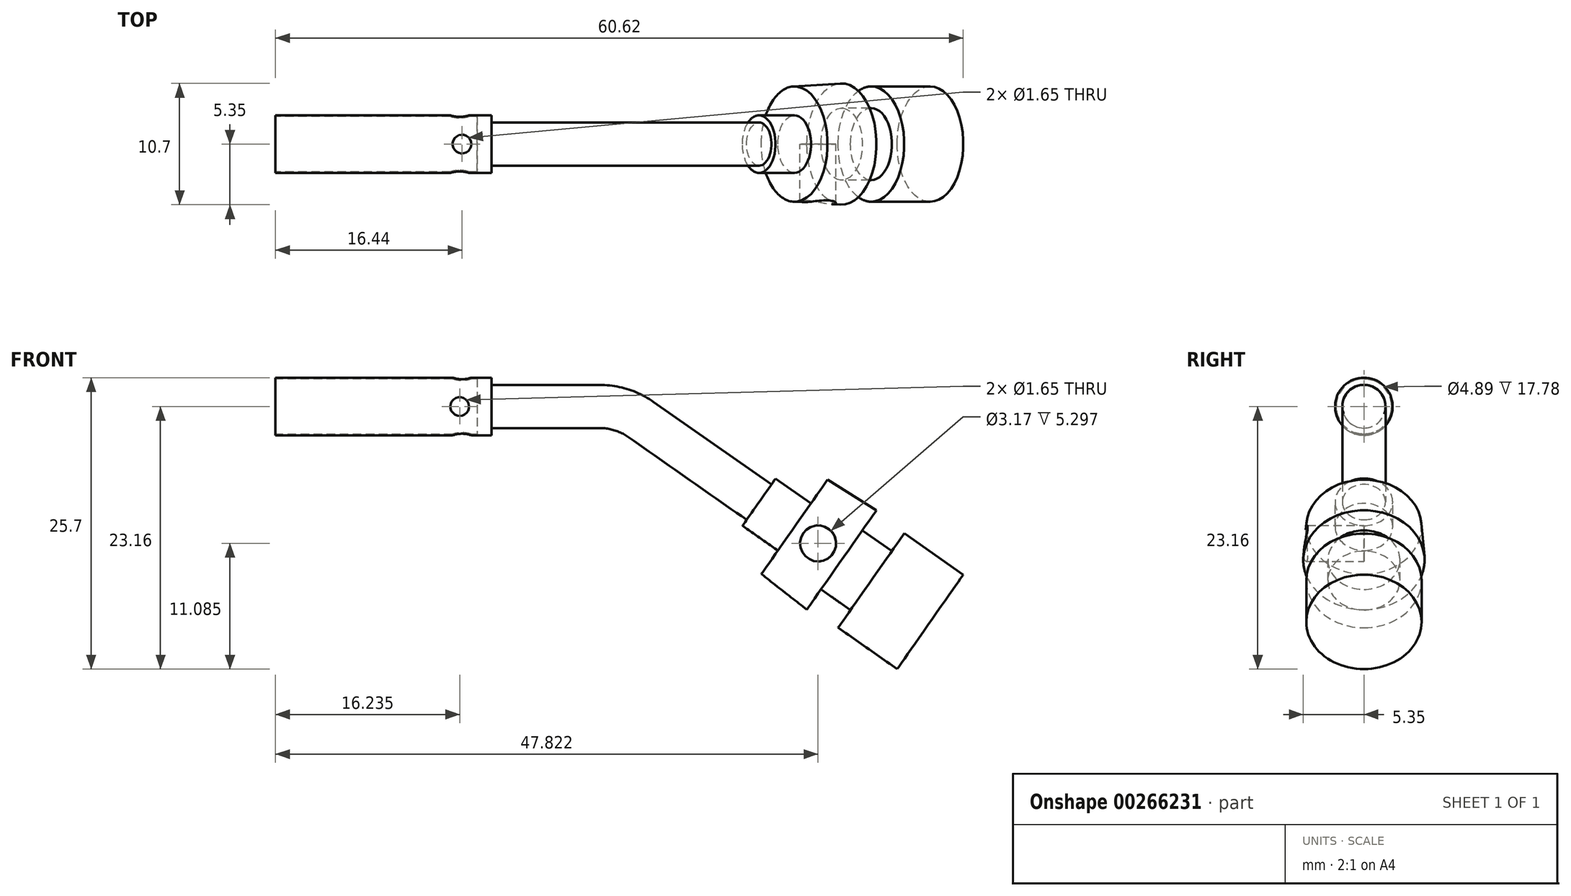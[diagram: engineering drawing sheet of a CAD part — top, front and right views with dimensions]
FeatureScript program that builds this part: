
annotation { "Feature Type Name" : "Feature", "Feature Type Description" : "" }
export const myFeature = defineFeature(function(context is Context, id is Id, definition is map)
    precondition{}
    {
        {
            var Q0;
            Q0=qCreatedBy(makeId("Right.planeOp"),FACE);
            var sketch = newSketch(context, id + "F0", { "sketchPlane" : qUnion([Q0])});
            skCircle(sketch, "E0", {"center": v(0, 0) * mm, "radius": 2.54 * mm});
            skSolve(sketch);
        }
        {
            var Q0;
            Q0=makeQuery(id+"F0.imprint","IMPRINT",FACE,{"disambiguationData":[TD([[makeQuery(id+"F0.imprint","IMPRINT",EDGE,{"derivedFrom":sQuery(id+"F0.wireOp",EDGE,"E0")}),1.0]])]});
            extrude(context, id + "F1", {"entities" : qUnion([Q0]), "depth" : 19.05 * mm});
        }
        {
            var Q0;
            Q0=makeQuery(id+"F1.opExtrude","CAP_FACE",FACE,{"disambiguationData":[OSD([sQuery(id+"F0.wireOp",EDGE,"E0")])],"isStart":false});
            var sketch = newSketch(context, id + "F2", { "sketchPlane" : qUnion([Q0])});
            skCircle(sketch, "E1", {"center": v(0, 0) * mm, "radius": 1.9 * mm});
            skSolve(sketch);
        }
        {
            var Q0;
            Q0=qCreatedBy(makeId("Front.planeOp"),FACE);
            var sketch = newSketch(context, id + "F3", { "sketchPlane" : qUnion([Q0])});
            skLineSegment(sketch, "E2.0", {"start": v(19.05, 2.54) * mm, "end": v(19.05, -2.54) * mm, "construction": true});
            skLineSegment(sketch, "E3", {"start": v(19.05, 0) * mm, "end": v(28.58, 0) * mm});
            skArc(sketch, "E4", {"start": v(32.22, -1.15) * mm, "mid": v(30.48, -0.3) * mm, "end": v(28.58, 0) * mm});
            skLineSegment(sketch, "E5", {"start": v(32.22, -1.15) * mm, "end": v(42.62, -8.43) * mm});
            skSolve(sketch);
        }
        {
            var Q0;
            Q0=makeQuery(id+"F2.imprint","IMPRINT",FACE,{"disambiguationData":[TD([[makeQuery(id+"F2.imprint","IMPRINT",EDGE,{"derivedFrom":sQuery(id+"F2.wireOp",EDGE,"E1")}),1.0]])]});
            var Q1;
            Q1=sQuery(id+"F3.wireOp",EDGE,"E3");
            var Q2;
            Q2=sQuery(id+"F3.wireOp",EDGE,"E4");
            var Q3;
            Q3=sQuery(id+"F3.wireOp",EDGE,"E5");
            sweep(context, id + "F4", {"operationType" : NewBodyOperationType.ADD, "profiles" : qUnion([Q0]), "path" : qUnion([Q1, Q2, Q3])});
        }
        {
            var Q0;
            Q0=makeQuery(id+"F4.opSweep","CAP_FACE",FACE,{"disambiguationData":[OSD([sQuery(id+"F2.wireOp",EDGE,"E1"),sQuery(id+"F3.wireOp",VERTEX,"E5.end")])],"isStart":false});
            var sketch = newSketch(context, id + "F5", { "sketchPlane" : qUnion([Q0])});
            skCircle(sketch, "E6", {"center": v(0, 17.54) * mm, "radius": 2.54 * mm});
            skSolve(sketch);
        }
        {
            var Q0;
            Q0=makeQuery(id+"F5.imprint","IMPRINT",FACE,{"disambiguationData":[TD([[makeQuery(id+"F5.imprint","IMPRINT",EDGE,{"derivedFrom":sQuery(id+"F5.wireOp",EDGE,"E6")}),1.0]])]});
            var Q1;
            Q1=makeQuery(id+"F5.imprint","IMPRINT",FACE,{"disambiguationData":[TD([[makeQuery(id+"F5.imprint","IMPRINT",EDGE,{"derivedFrom":makeQuery(id+"F4.opSweep","CAP_EDGE",EDGE,{"disambiguationData":[OSD([sQuery(id+"F2.wireOp",EDGE,"E1"),sQuery(id+"F3.wireOp",VERTEX,"E5.end")])],"isStart":false})}),1.0]])]});
            extrude(context, id + "F6", {"entities" : qUnion([Q0, Q1]), "operationType" : NewBodyOperationType.ADD, "depth" : 3.8 * mm});
        }
        {
            var Q0;
            Q0=makeQuery(id+"F6.opExtrude","CAP_FACE",FACE,{"disambiguationData":[OSD([sQuery(id+"F5.wireOp",EDGE,"E6")])],"isStart":false});
            var sketch = newSketch(context, id + "F7", { "sketchPlane" : qUnion([Q0])});
            skCircle(sketch, "E7", {"center": v(0, 17.54) * mm, "radius": 5.08 * mm});
            skSolve(sketch);
        }
        {
            var Q0;
            Q0=makeQuery(id+"F7.imprint","IMPRINT",FACE,{"disambiguationData":[TD([[makeQuery(id+"F7.imprint","IMPRINT",EDGE,{"derivedFrom":makeQuery(id+"F6.opExtrude","CAP_EDGE",EDGE,{"disambiguationData":[OSD([sQuery(id+"F5.wireOp",EDGE,"E6")])],"isStart":false})}),1.0]])]});
            var Q1;
            Q1=makeQuery(id+"F7.imprint","IMPRINT",FACE,{"disambiguationData":[TD([[makeQuery(id+"F7.imprint","IMPRINT",EDGE,{"derivedFrom":sQuery(id+"F7.wireOp",EDGE,"E7")}),1.0]])]});
            extrude(context, id + "F8", {"entities" : qUnion([Q0, Q1]), "operationType" : NewBodyOperationType.ADD, "depth" : 5.08 * mm, "hasDraft" : true, "draftAngle" : 3 * degree});
        }
        {
            var Q0;
            Q0=makeQuery(id+"F8.opExtrude","CAP_FACE",FACE,{"disambiguationData":[OSD([sQuery(id+"F7.wireOp",EDGE,"E7")])],"isStart":false});
            var sketch = newSketch(context, id + "F9", { "sketchPlane" : qUnion([Q0])});
            skCircle(sketch, "E8", {"center": v(0, 17.54) * mm, "radius": 3.18 * mm});
            skSolve(sketch);
        }
        {
            var Q0;
            Q0=makeQuery(id+"F9.imprint","IMPRINT",FACE,{"disambiguationData":[TD([[makeQuery(id+"F9.imprint","IMPRINT",EDGE,{"derivedFrom":sQuery(id+"F9.wireOp",EDGE,"E8")}),1.0]])]});
            extrude(context, id + "F10", {"entities" : qUnion([Q0]), "operationType" : NewBodyOperationType.ADD, "depth" : 3.17 * mm});
        }
        {
            var Q0;
            Q0=makeQuery(id+"F10.opExtrude","CAP_FACE",FACE,{"disambiguationData":[OSD([sQuery(id+"F9.wireOp",EDGE,"E8")])],"isStart":false});
            var sketch = newSketch(context, id + "F11", { "sketchPlane" : qUnion([Q0])});
            skCircle(sketch, "E9", {"center": v(0, 17.54) * mm, "radius": 5.08 * mm});
            skSolve(sketch);
        }
        {
            var Q0;
            Q0=makeQuery(id+"F11.imprint","IMPRINT",FACE,{"disambiguationData":[TD([[makeQuery(id+"F11.imprint","IMPRINT",EDGE,{"derivedFrom":sQuery(id+"F11.wireOp",EDGE,"E9")}),1.0]])]});
            var Q1;
            Q1=makeQuery(id+"F11.imprint","IMPRINT",FACE,{"disambiguationData":[TD([[makeQuery(id+"F11.imprint","IMPRINT",EDGE,{"derivedFrom":makeQuery(id+"F10.opExtrude","CAP_EDGE",EDGE,{"disambiguationData":[OSD([sQuery(id+"F9.wireOp",EDGE,"E8")])],"isStart":false})}),1.0]])]});
            extrude(context, id + "F12", {"entities" : qUnion([Q0, Q1]), "operationType" : NewBodyOperationType.ADD, "depth" : 6.35 * mm});
        }
        {
            var Q0;
            Q0=makeQuery(id+"F1.opExtrude","CAP_FACE",FACE,{"disambiguationData":[OSD([sQuery(id+"F0.wireOp",EDGE,"E0")])],"isStart":true});
            var sketch = newSketch(context, id + "F13", { "sketchPlane" : qUnion([Q0])});
            skCircle(sketch, "E10", {"center": v(0, 0) * mm, "radius": 2.44 * mm});
            skSolve(sketch);
        }
        {
            var Q0;
            Q0=makeQuery(id+"F13.imprint","IMPRINT",FACE,{"disambiguationData":[TD([[makeQuery(id+"F13.imprint","IMPRINT",EDGE,{"derivedFrom":sQuery(id+"F13.wireOp",EDGE,"E10")}),1.0]])]});
            extrude(context, id + "F14", {"entities" : qUnion([Q0]), "operationType" : NewBodyOperationType.REMOVE, "oppositeDirection" : true, "depth" : 17.78 * mm});
        }
        {
            var Q0;
            Q0=qCreatedBy(makeId("Top.planeOp"),FACE);
            var sketch = newSketch(context, id + "F15", { "sketchPlane" : qUnion([Q0])});
            skLineSegment(sketch, "E11", {"start": v(0, 2.54) * mm, "end": v(18.98, 2.54) * mm, "construction": true});
            skLineSegment(sketch, "E12", {"start": v(19.05, -2.54) * mm, "end": v(0, -2.54) * mm, "construction": true});
            skCircle(sketch, "E13", {"center": v(16.44, 0) * mm, "radius": 0.83 * mm});
            skSolve(sketch);
        }
        {
            var Q0;
            Q0=makeQuery(id+"F15.imprint","IMPRINT",FACE,{"disambiguationData":[TD([[makeQuery(id+"F15.imprint","IMPRINT",EDGE,{"derivedFrom":sQuery(id+"F15.wireOp",EDGE,"E13")}),1.0]])]});
            extrude(context, id + "F16", {"entities" : qUnion([Q0]), "operationType" : NewBodyOperationType.REMOVE, "endBound" : BoundingType.THROUGH_ALL, "oppositeDirection" : true, "depth" : 25.4 * mm, "hasSecondDirection" : true, "secondDirectionBound" : SecondDirectionBoundingType.THROUGH_ALL, "secondDirectionOppositeDirection" : false, "secondDirectionDepth" : 25.4 * mm});
        }
        {
            var Q0;
            Q0=qCreatedBy(makeId("Front.planeOp"),FACE);
            var sketch = newSketch(context, id + "F17", { "sketchPlane" : qUnion([Q0])});
            skLineSegment(sketch, "E14", {"start": v(0, 2.54) * mm, "end": v(19.05, 2.54) * mm, "construction": true});
            skLineSegment(sketch, "E15", {"start": v(18.78, -2.54) * mm, "end": v(0, -2.54) * mm, "construction": true});
            skCircle(sketch, "E16", {"center": v(16.24, 0) * mm, "radius": 0.83 * mm});
            skSolve(sketch);
        }
        {
            var Q0;
            Q0=makeQuery(id+"F17.imprint","IMPRINT",FACE,{"disambiguationData":[TD([[makeQuery(id+"F17.imprint","IMPRINT",EDGE,{"derivedFrom":sQuery(id+"F17.wireOp",EDGE,"E16")}),1.0]])]});
            extrude(context, id + "F18", {"entities" : qUnion([Q0]), "operationType" : NewBodyOperationType.REMOVE, "endBound" : BoundingType.THROUGH_ALL, "oppositeDirection" : true, "depth" : 25.4 * mm, "hasSecondDirection" : true, "secondDirectionBound" : SecondDirectionBoundingType.THROUGH_ALL, "secondDirectionOppositeDirection" : false, "secondDirectionDepth" : 25.4 * mm});
        }
        {
            var Q0;
            Q0=qCreatedBy(makeId("Front.planeOp"),FACE);
            var sketch = newSketch(context, id + "F19", { "sketchPlane" : qUnion([Q0])});
            skLineSegment(sketch, "E17", {"start": v(46.84, -17.91) * mm, "end": v(42.83, -14.78) * mm, "construction": true});
            skLineSegment(sketch, "E18", {"start": v(48.66, -6.46) * mm, "end": v(52.97, -9.15) * mm, "construction": true});
            skLineSegment(sketch, "E19", {"start": v(44.83, -16.35) * mm, "end": v(50.81, -7.8) * mm, "construction": true});
            skCircle(sketch, "E20", {"center": v(47.82, -12.08) * mm, "radius": 1.59 * mm});
            skSolve(sketch);
        }
        {
            var Q0;
            Q0=qSketchRegion(id+"F19",true);
            extrude(context, id + "F20", {"entities" : qUnion([Q0]), "operationType" : NewBodyOperationType.REMOVE, "endBound" : BoundingType.THROUGH_ALL, "depth" : 25.4 * mm});
        }
    });
